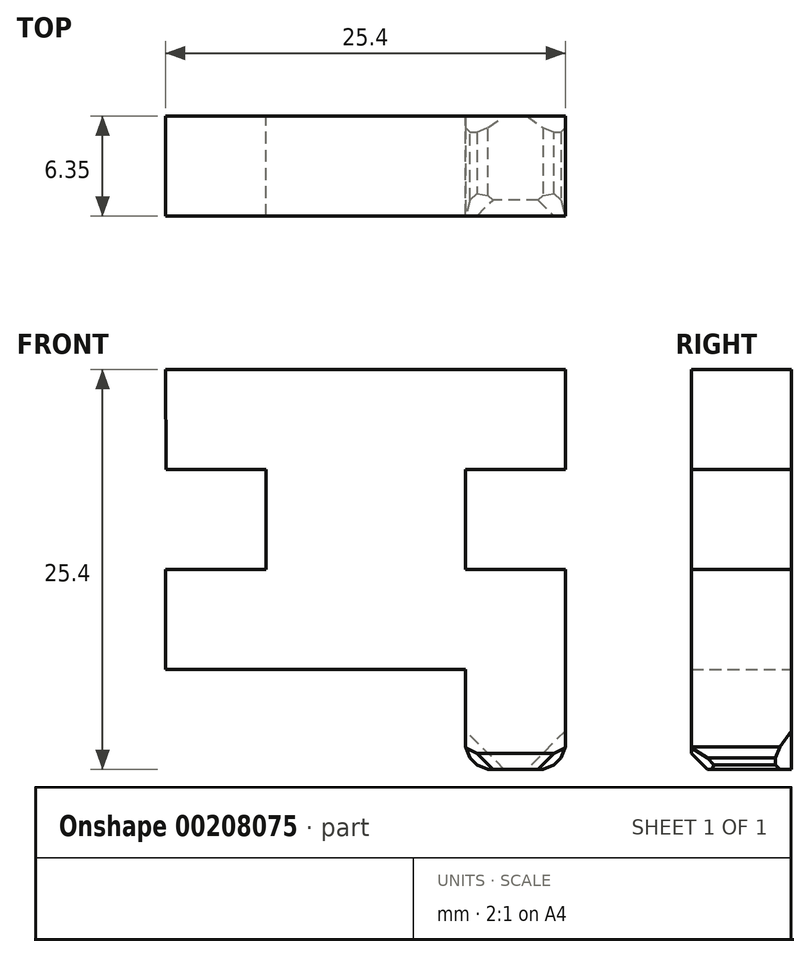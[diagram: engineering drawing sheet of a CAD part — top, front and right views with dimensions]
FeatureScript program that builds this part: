
annotation { "Feature Type Name" : "Feature", "Feature Type Description" : "" }
export const myFeature = defineFeature(function(context is Context, id is Id, definition is map)
    precondition{}
    {
        {
            var Q0;
            Q0=qCreatedBy(makeId("Front.planeOp"),FACE);
            var sketch = newSketch(context, id + "F0", { "sketchPlane" : qUnion([Q0])});
            skLineSegment(sketch, "E0.bottom", {"start": v(0, 0) * mm, "end": v(25.4, 0) * mm});
            skLineSegment(sketch, "E0.top", {"start": v(0, -25.4) * mm, "end": v(25.4, -25.4) * mm});
            skLineSegment(sketch, "E0.right", {"start": v(25.4, 0) * mm, "end": v(25.4, -25.4) * mm});
            skLineSegment(sketch, "E1", {"start": v(25.4, -25.4) * mm, "end": v(25.4, -12.7) * mm});
            skLineSegment(sketch, "E2", {"start": v(19.05, -25.4) * mm, "end": v(19.05, -19.05) * mm});
            skLineSegment(sketch, "E3", {"start": v(19.05, -19.05) * mm, "end": v(0, -19.05) * mm});
            skLineSegment(sketch, "E4", {"start": v(25.4, -12.7) * mm, "end": v(19.05, -12.7) * mm});
            skLineSegment(sketch, "E5", {"start": v(19.05, -12.7) * mm, "end": v(19.05, -6.35) * mm});
            skLineSegment(sketch, "E6", {"start": v(19.05, -6.35) * mm, "end": v(25.4, -6.35) * mm});
            skLineSegment(sketch, "E7", {"start": v(0, -12.7) * mm, "end": v(6.37, -12.7) * mm});
            skLineSegment(sketch, "E8", {"start": v(6.37, -12.7) * mm, "end": v(6.37, -6.35) * mm});
            skLineSegment(sketch, "E9", {"start": v(0.02, -6.35) * mm, "end": v(6.37, -6.35) * mm});
            skLineSegment(sketch, "E10", {"start": v(0, 0) * mm, "end": v(0.02, -6.35) * mm});
            skLineSegment(sketch, "E11", {"start": v(0, -19.05) * mm, "end": v(0, -12.7) * mm});
            skSolve(sketch);
        }
        {
            var Q0;
            {var subQ0=sQuery(id+"F0.wireOp",EDGE,"E0.bottom");Q0=makeQuery(id+"F0.imprint","IMPRINT",FACE,{"disambiguationData":[TD([[makeQuery(id+"F0.imprint","IMPRINT",EDGE,{"derivedFrom":subQ0}),-1.0]])]});}
            extrude(context, id + "F1", {"entities" : qUnion([Q0]), "depth" : 6.35 * mm});
        }
        {
            var Q0;
            Q0=makeQuery(id+"F1.opExtrude","CAP_EDGE",EDGE,{"disambiguationData":[OSD([sQuery(id+"F0.wireOp",EDGE,"E0.top")])],"isStart":false});
            chamfer(context, id + "F2", {"entities" : qUnion([Q0]), "width" : 1.02 * mm, "tangentPropagation" : true});
        }
        {
            var Q0;
            Q0=makeQuery(id+"F1.opExtrude","SWEPT_EDGE",EDGE,{"disambiguationData":[OSD([sQuery(id+"F0.wireOp",EDGE,"E0.top"),sQuery(id+"F0.wireOp",EDGE,"E1")])]});
            chamfer(context, id + "F3", {"entities" : qUnion([Q0]), "width" : 1.02 * mm, "tangentPropagation" : true});
        }
        {
            var Q0;
            Q0=makeQuery(id+"F3.opChamfer","BLEND_FACE",FACE,{"disambiguationData":[OSD([sQuery(id+"F0.wireOp",EDGE,"E0.top"),sQuery(id+"F0.wireOp",EDGE,"E1")])]});
            chamfer(context, id + "F4", {"entities" : qUnion([Q0]), "width" : 1.02 * mm});
        }
    });
